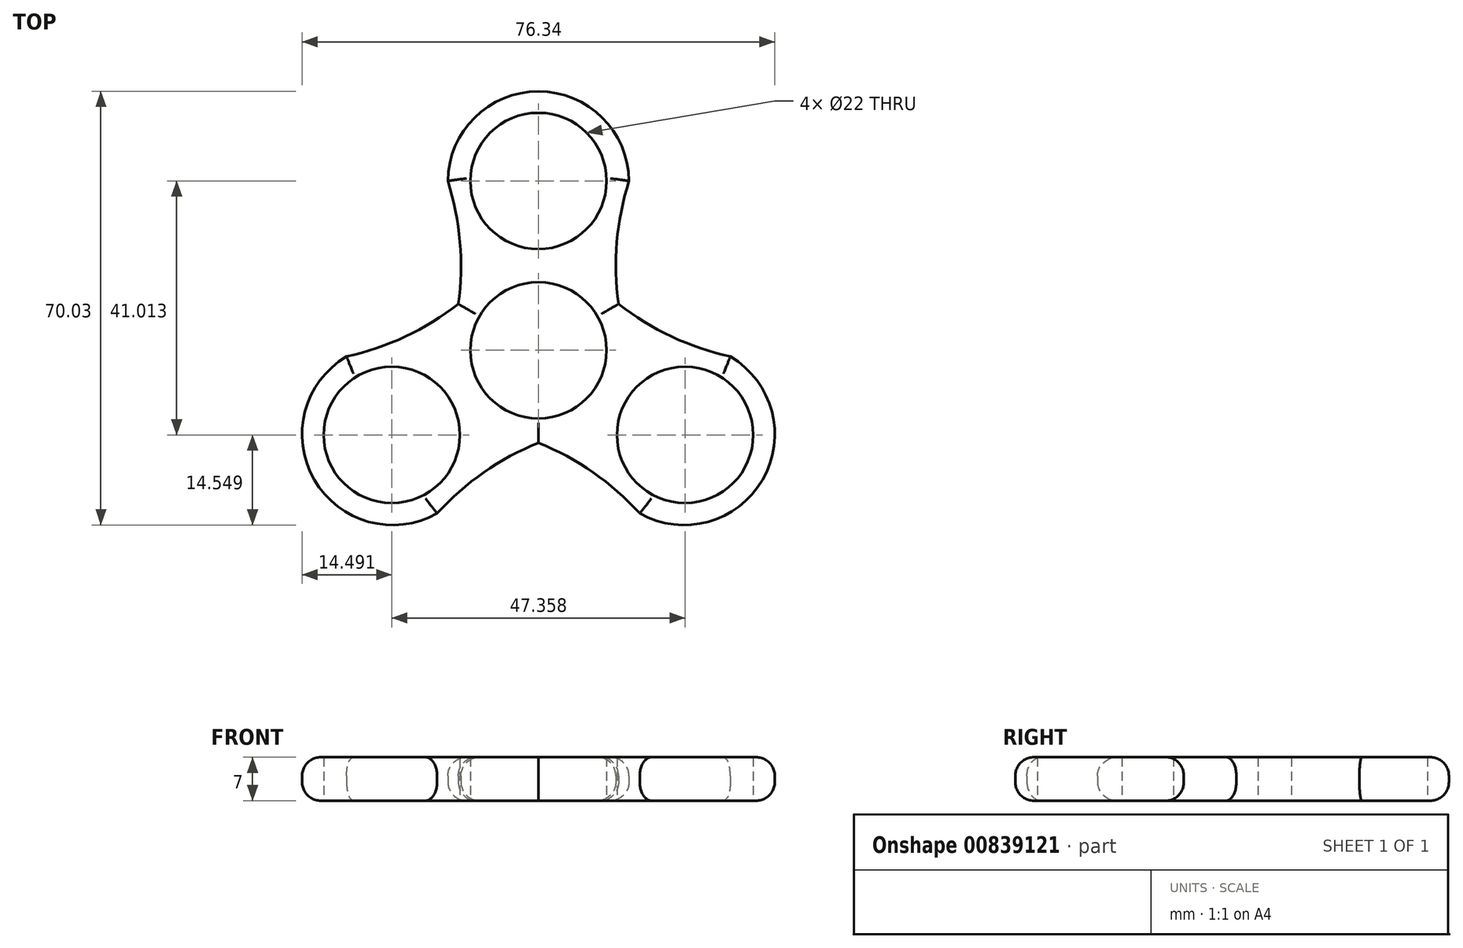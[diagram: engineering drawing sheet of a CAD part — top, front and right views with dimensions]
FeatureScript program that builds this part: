
annotation { "Feature Type Name" : "Feature", "Feature Type Description" : "" }
export const myFeature = defineFeature(function(context is Context, id is Id, definition is map)
    precondition{}
    {
        {
            var Q0;
            Q0=qCreatedBy(makeId("Top.planeOp"),FACE);
            var sketch = newSketch(context, id + "F0", { "sketchPlane" : qUnion([Q0])});
            skCircle(sketch, "E0", {"center": v(0, 0) * mm, "radius": 11 * mm});
            skCircle(sketch, "E1", {"center": v(0, 27.34) * mm, "radius": 11 * mm});
            skArc(sketch, "E2", {"start": v(14.63, 27.34) * mm, "mid": v(0, 41.81) * mm, "end": v(-14.63, 27.34) * mm});
            skArc(sketch, "E3", {"start": v(-14.63, 0) * mm, "mid": v(-12.5, 13.67) * mm, "end": v(-14.63, 27.34) * mm});
            skArc(sketch, "E4", {"start": v(14.63, 27.34) * mm, "mid": v(12.5, 13.67) * mm, "end": v(14.63, 0) * mm});
            skArc(sketch, "E5.1.0", {"start": v(-31, -1) * mm, "mid": v(-36.2, -20.9) * mm, "end": v(-16.36, -26.34) * mm});
            skCircle(sketch, "E5.1.1", {"center": v(-23.68, -13.67) * mm, "radius": 11 * mm});
            skArc(sketch, "E5.1.2", {"start": v(7.32, -12.67) * mm, "mid": v(-5.59, -17.67) * mm, "end": v(-16.36, -26.34) * mm});
            skArc(sketch, "E5.1.3", {"start": v(-31, -1) * mm, "mid": v(-18.1, 4) * mm, "end": v(-7.32, 12.67) * mm});
            skArc(sketch, "E5.2.0", {"start": v(16.36, -26.34) * mm, "mid": v(36.2, -20.9) * mm, "end": v(31, -1) * mm});
            skCircle(sketch, "E5.2.1", {"center": v(23.68, -13.67) * mm, "radius": 11 * mm});
            skArc(sketch, "E5.2.2", {"start": v(7.32, 12.67) * mm, "mid": v(18.1, 4) * mm, "end": v(31, -1) * mm});
            skArc(sketch, "E5.2.3", {"start": v(16.36, -26.34) * mm, "mid": v(5.59, -17.67) * mm, "end": v(-7.32, -12.67) * mm});
            skSolve(sketch);
        }
        {
            var Q0;
            Q0 = qSketchRegion(id + "F0", true);
            extrude(context, id + "F1", {"entities" : qUnion([Q0]), "depth" : 7 * mm, "offsetDistance" : 25 * mm});
        }
        {
            var Q0;
            Q0=makeQuery(id+"F1.opExtrude","CAP_EDGE",EDGE,{"disambiguationData":[OSD([sQuery(id+"F0.wireOp",EDGE,"E3")])],"isStart":false});
            var Q1;
            Q1=makeQuery(id+"F1.opExtrude","CAP_EDGE",EDGE,{"disambiguationData":[OSD([sQuery(id+"F0.wireOp",EDGE,"E2")])],"isStart":false});
            var Q2;
            Q2=makeQuery(id+"F1.opExtrude","CAP_EDGE",EDGE,{"disambiguationData":[OSD([sQuery(id+"F0.wireOp",EDGE,"E4")])],"isStart":false});
            var Q3;
            Q3=makeQuery(id+"F1.opExtrude","CAP_EDGE",EDGE,{"disambiguationData":[OSD([sQuery(id+"F0.wireOp",EDGE,"E5.2.2")])],"isStart":false});
            var Q4;
            Q4=makeQuery(id+"F1.opExtrude","CAP_EDGE",EDGE,{"disambiguationData":[OSD([sQuery(id+"F0.wireOp",EDGE,"E5.2.0")])],"isStart":false});
            var Q5;
            Q5=makeQuery(id+"F1.opExtrude","CAP_EDGE",EDGE,{"disambiguationData":[OSD([sQuery(id+"F0.wireOp",EDGE,"E5.2.3")])],"isStart":false});
            var Q6;
            Q6=makeQuery(id+"F1.opExtrude","CAP_EDGE",EDGE,{"disambiguationData":[OSD([sQuery(id+"F0.wireOp",EDGE,"E5.1.2")])],"isStart":false});
            var Q7;
            Q7=makeQuery(id+"F1.opExtrude","CAP_EDGE",EDGE,{"disambiguationData":[OSD([sQuery(id+"F0.wireOp",EDGE,"E5.1.0")])],"isStart":false});
            var Q8;
            Q8=makeQuery(id+"F1.opExtrude","CAP_EDGE",EDGE,{"disambiguationData":[OSD([sQuery(id+"F0.wireOp",EDGE,"E5.1.3")])],"isStart":false});
            fillet(context, id + "F2", {"entities" : qUnion([Q0, Q1, Q2, Q3, Q4, Q5, Q6, Q7, Q8]), "radius" : 3 * mm, "tangentPropagation" : true, "allowEdgeOverflow" : false});
        }
        {
            var Q0;
            Q0=makeQuery(id+"F1.opExtrude","CAP_EDGE",EDGE,{"disambiguationData":[OSD([sQuery(id+"F0.wireOp",EDGE,"E3")])],"isStart":true});
            var Q1;
            Q1=makeQuery(id+"F1.opExtrude","CAP_EDGE",EDGE,{"disambiguationData":[OSD([sQuery(id+"F0.wireOp",EDGE,"E2")])],"isStart":true});
            var Q2;
            Q2=makeQuery(id+"F1.opExtrude","CAP_EDGE",EDGE,{"disambiguationData":[OSD([sQuery(id+"F0.wireOp",EDGE,"E4")])],"isStart":true});
            var Q3;
            Q3=makeQuery(id+"F1.opExtrude","CAP_EDGE",EDGE,{"disambiguationData":[OSD([sQuery(id+"F0.wireOp",EDGE,"E5.2.2")])],"isStart":true});
            var Q4;
            Q4=makeQuery(id+"F1.opExtrude","CAP_EDGE",EDGE,{"disambiguationData":[OSD([sQuery(id+"F0.wireOp",EDGE,"E5.2.0")])],"isStart":true});
            var Q5;
            Q5=makeQuery(id+"F1.opExtrude","CAP_EDGE",EDGE,{"disambiguationData":[OSD([sQuery(id+"F0.wireOp",EDGE,"E5.2.3")])],"isStart":true});
            var Q6;
            Q6=makeQuery(id+"F1.opExtrude","CAP_EDGE",EDGE,{"disambiguationData":[OSD([sQuery(id+"F0.wireOp",EDGE,"E5.1.2")])],"isStart":true});
            var Q7;
            Q7=makeQuery(id+"F1.opExtrude","CAP_EDGE",EDGE,{"disambiguationData":[OSD([sQuery(id+"F0.wireOp",EDGE,"E5.1.0")])],"isStart":true});
            var Q8;
            Q8=makeQuery(id+"F1.opExtrude","CAP_EDGE",EDGE,{"disambiguationData":[OSD([sQuery(id+"F0.wireOp",EDGE,"E5.1.3")])],"isStart":true});
            fillet(context, id + "F3", {"entities" : qUnion([Q0, Q1, Q2, Q3, Q4, Q5, Q6, Q7, Q8]), "radius" : 3 * mm, "tangentPropagation" : true, "allowEdgeOverflow" : false});
        }
    });
